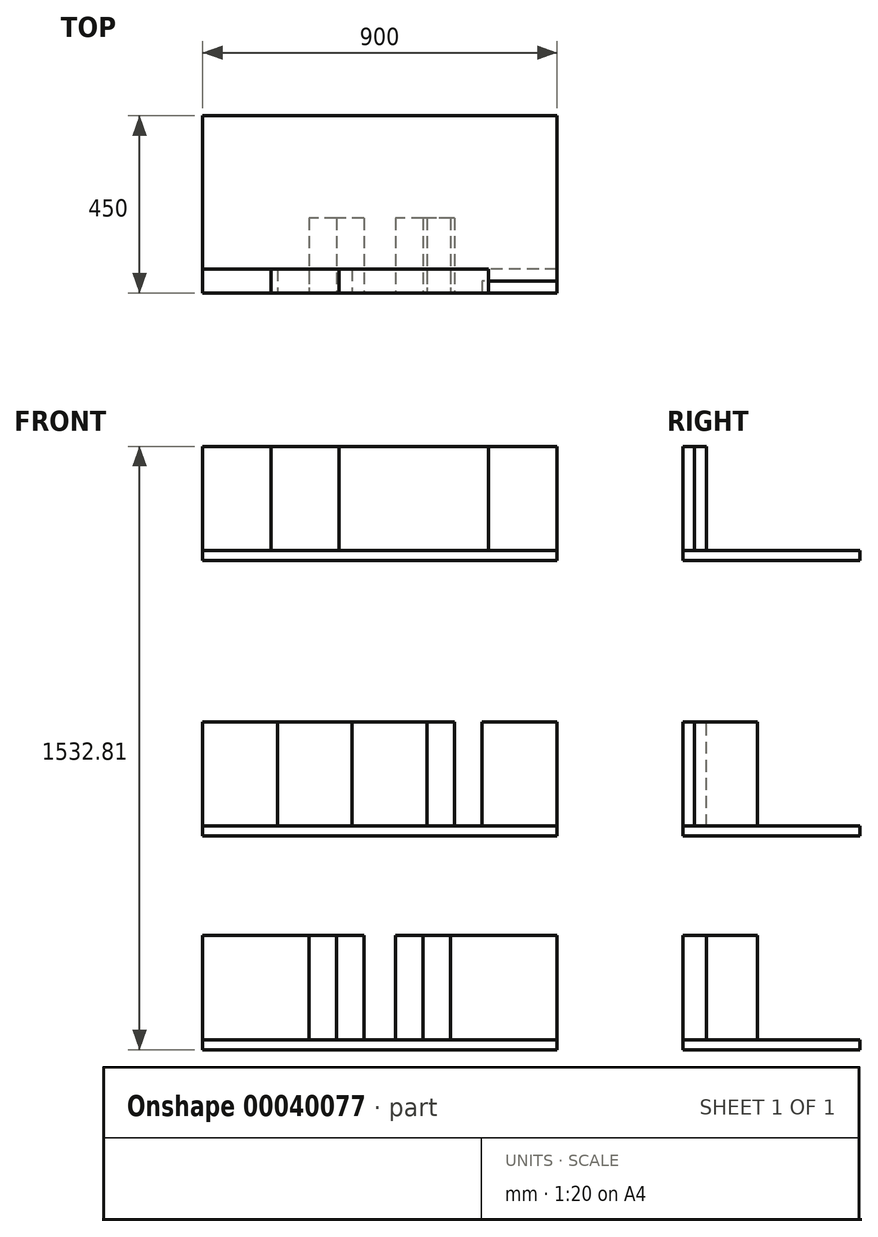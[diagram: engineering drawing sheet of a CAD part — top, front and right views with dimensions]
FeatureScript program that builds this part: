
annotation { "Feature Type Name" : "Feature", "Feature Type Description" : "" }
export const myFeature = defineFeature(function(context is Context, id is Id, definition is map)
    precondition{}
    {
        {
            var Q0;
            Q0=qCreatedBy(makeId("Front.planeOp"),FACE);
            var sketch = newSketch(context, id + "F0", { "sketchPlane" : qUnion([Q0])});
            skLineSegment(sketch, "E0.bottom", {"start": v(483.33, -12.5) * mm, "end": v(-416.67, -12.5) * mm});
            skLineSegment(sketch, "E0.top", {"start": v(483.33, 12.5) * mm, "end": v(-416.67, 12.5) * mm});
            skLineSegment(sketch, "E0.left", {"start": v(483.33, -12.5) * mm, "end": v(483.33, 12.5) * mm});
            skLineSegment(sketch, "E0.right", {"start": v(-416.67, -12.5) * mm, "end": v(-416.67, 12.5) * mm});
            skLineSegment(sketch, "E1.top", {"start": v(-416.67, 277.5) * mm, "end": v(-243.33, 277.5) * mm});
            skLineSegment(sketch, "E1.left", {"start": v(-416.67, 12.5) * mm, "end": v(-416.67, 277.5) * mm});
            skLineSegment(sketch, "E1.right", {"start": v(-243.33, 12.5) * mm, "end": v(-243.33, 277.5) * mm});
            skLineSegment(sketch, "E2.bottom", {"start": v(-243.33, 12.5) * mm, "end": v(-70, 12.5) * mm});
            skLineSegment(sketch, "E2.top", {"start": v(-243.33, 277.5) * mm, "end": v(-70, 277.5) * mm});
            skLineSegment(sketch, "E2.right", {"start": v(-70, 12.5) * mm, "end": v(-70, 277.5) * mm});
            skLineSegment(sketch, "E3.bottom", {"start": v(-70, 12.5) * mm, "end": v(310, 12.5) * mm});
            skLineSegment(sketch, "E3.top", {"start": v(-70, 277.5) * mm, "end": v(310, 277.5) * mm});
            skLineSegment(sketch, "E3.right", {"start": v(310, 12.5) * mm, "end": v(310, 277.5) * mm});
            skLineSegment(sketch, "E4.bottom", {"start": v(310, 277.5) * mm, "end": v(483.33, 277.5) * mm});
            skLineSegment(sketch, "E4.top", {"start": v(310, 12.5) * mm, "end": v(483.33, 12.5) * mm});
            skLineSegment(sketch, "E4.left", {"start": v(310, 277.5) * mm, "end": v(310, 12.5) * mm});
            skLineSegment(sketch, "E4.right", {"start": v(483.33, 277.5) * mm, "end": v(483.33, 12.5) * mm});
            skLineSegment(sketch, "E5.bottom", {"start": v(483.33, -712.13) * mm, "end": v(-416.67, -712.13) * mm});
            skLineSegment(sketch, "E5.top", {"start": v(483.33, -687.13) * mm, "end": v(-416.67, -687.13) * mm});
            skLineSegment(sketch, "E5.left", {"start": v(483.33, -712.13) * mm, "end": v(483.33, -687.13) * mm});
            skLineSegment(sketch, "E5.right", {"start": v(-416.67, -712.13) * mm, "end": v(-416.67, -687.13) * mm});
            skLineSegment(sketch, "E6.top", {"start": v(-416.67, -422.13) * mm, "end": v(-226.67, -422.13) * mm});
            skLineSegment(sketch, "E6.left", {"start": v(-416.67, -687.13) * mm, "end": v(-416.67, -422.13) * mm});
            skLineSegment(sketch, "E6.right", {"start": v(-226.67, -687.13) * mm, "end": v(-226.67, -422.13) * mm});
            skLineSegment(sketch, "E7.bottom", {"start": v(-226.67, -687.13) * mm, "end": v(-36.67, -687.13) * mm});
            skLineSegment(sketch, "E7.top", {"start": v(-226.67, -422.13) * mm, "end": v(-36.67, -422.13) * mm});
            skLineSegment(sketch, "E7.right", {"start": v(-36.67, -687.13) * mm, "end": v(-36.67, -422.13) * mm});
            skLineSegment(sketch, "E8.bottom", {"start": v(-36.67, -687.13) * mm, "end": v(293.33, -687.13) * mm});
            skLineSegment(sketch, "E8.right", {"start": v(293.33, -687.13) * mm, "end": v(293.33, -422.13) * mm});
            skLineSegment(sketch, "E9.bottom", {"start": v(293.33, -422.13) * mm, "end": v(483.33, -422.13) * mm});
            skLineSegment(sketch, "E9.top", {"start": v(293.33, -687.13) * mm, "end": v(483.33, -687.13) * mm});
            skLineSegment(sketch, "E9.left", {"start": v(293.33, -422.13) * mm, "end": v(293.33, -687.13) * mm});
            skLineSegment(sketch, "E9.right", {"start": v(483.33, -422.13) * mm, "end": v(483.33, -687.13) * mm});
            skLineSegment(sketch, "E10", {"start": v(-36.67, -422.13) * mm, "end": v(153.33, -422.13) * mm});
            skLineSegment(sketch, "E11", {"start": v(153.33, -422.13) * mm, "end": v(153.33, -687.13) * mm});
            skLineSegment(sketch, "E12.bottom", {"start": v(153.33, -687.13) * mm, "end": v(223.33, -687.13) * mm});
            skLineSegment(sketch, "E12.top", {"start": v(153.33, -422.13) * mm, "end": v(223.33, -422.13) * mm});
            skLineSegment(sketch, "E12.left", {"start": v(153.33, -687.13) * mm, "end": v(153.33, -422.13) * mm});
            skLineSegment(sketch, "E12.right", {"start": v(223.33, -687.13) * mm, "end": v(223.33, -422.13) * mm});
            skLineSegment(sketch, "E13.bottom", {"start": v(483.33, -1255.31) * mm, "end": v(-416.67, -1255.31) * mm});
            skLineSegment(sketch, "E13.top", {"start": v(483.33, -1230.31) * mm, "end": v(-416.67, -1230.31) * mm});
            skLineSegment(sketch, "E13.left", {"start": v(483.33, -1255.31) * mm, "end": v(483.33, -1230.31) * mm});
            skLineSegment(sketch, "E13.right", {"start": v(-416.67, -1255.31) * mm, "end": v(-416.67, -1230.31) * mm});
            skLineSegment(sketch, "E14.top", {"start": v(-416.67, -965.31) * mm, "end": v(-146.67, -965.31) * mm});
            skLineSegment(sketch, "E14.left", {"start": v(-416.67, -1230.31) * mm, "end": v(-416.67, -965.31) * mm});
            skLineSegment(sketch, "E14.right", {"start": v(-146.67, -1230.31) * mm, "end": v(-146.67, -965.31) * mm});
            skLineSegment(sketch, "E15.bottom", {"start": v(-146.67, -1230.31) * mm, "end": v(-76.67, -1230.31) * mm});
            skLineSegment(sketch, "E15.top", {"start": v(-146.67, -965.31) * mm, "end": v(-76.67, -965.31) * mm});
            skLineSegment(sketch, "E15.right", {"start": v(-76.67, -1230.31) * mm, "end": v(-76.67, -965.31) * mm});
            skLineSegment(sketch, "E16.bottom", {"start": v(-76.67, -1230.31) * mm, "end": v(-6.67, -1230.31) * mm});
            skLineSegment(sketch, "E16.top", {"start": v(-76.67, -965.31) * mm, "end": v(-6.67, -965.31) * mm});
            skLineSegment(sketch, "E16.right", {"start": v(-6.67, -1230.31) * mm, "end": v(-6.67, -965.31) * mm});
            skLineSegment(sketch, "E17", {"start": v(33.33, -1230.31) * mm, "end": v(33.33, -895.3) * mm, "construction": true});
            skLineSegment(sketch, "E18.MirrorCS", {"start": v(73.33, -1230.31) * mm, "end": v(73.33, -965.31) * mm});
            skLineSegment(sketch, "E19.MirrorCS", {"start": v(143.33, -965.31) * mm, "end": v(73.33, -965.31) * mm});
            skLineSegment(sketch, "E20.MirrorCS", {"start": v(143.33, -1230.31) * mm, "end": v(143.33, -965.31) * mm});
            skLineSegment(sketch, "E21.MirrorCS", {"start": v(213.33, -965.31) * mm, "end": v(143.33, -965.31) * mm});
            skLineSegment(sketch, "E22.MirrorCS", {"start": v(213.33, -1230.31) * mm, "end": v(213.33, -965.31) * mm});
            skLineSegment(sketch, "E23.MirrorCS", {"start": v(483.33, -965.31) * mm, "end": v(213.33, -965.31) * mm});
            skLineSegment(sketch, "E24.MirrorCS", {"start": v(483.33, -1230.31) * mm, "end": v(483.33, -965.31) * mm});
            skSolve(sketch);
        }
        {
            var Q0;
            Q0=makeQuery(id+"F0.imprint","IMPRINT",FACE,{"disambiguationData":[TD([[makeQuery(id+"F0.imprint","IMPRINT",EDGE,{"derivedFrom":sQuery(id+"F0.wireOp",EDGE,"E0.bottom")}),-1.0]])]});
            var Q1;
            Q1=makeQuery(id+"F0.imprint","IMPRINT",FACE,{"disambiguationData":[TD([[makeQuery(id+"F0.imprint","IMPRINT",EDGE,{"derivedFrom":sQuery(id+"F0.wireOp",EDGE,"E5.bottom")}),-1.0]])]});
            var Q2;
            Q2=makeQuery(id+"F0.imprint","IMPRINT",FACE,{"disambiguationData":[TD([[makeQuery(id+"F0.imprint","IMPRINT",EDGE,{"derivedFrom":sQuery(id+"F0.wireOp",EDGE,"E13.bottom")}),-1.0]])]});
            extrude(context, id + "F1", {"entities" : qUnion([Q0, Q1, Q2]), "oppositeDirection" : true, "depth" : 450 * mm, "offsetDistance" : 25 * mm});
        }
        {
            var Q0;
            Q0=makeQuery(id+"F0.imprint","IMPRINT",FACE,{"disambiguationData":[TD([[makeQuery(id+"F0.imprint","IMPRINT",EDGE,{"derivedFrom":sQuery(id+"F0.wireOp",EDGE,"E1.top")}),-1.0]])]});
            var Q1;
            Q1=makeQuery(id+"F0.imprint","IMPRINT",FACE,{"disambiguationData":[TD([[makeQuery(id+"F0.imprint","IMPRINT",EDGE,{"derivedFrom":sQuery(id+"F0.wireOp",EDGE,"E6.top")}),-1.0]])]});
            var Q2;
            {var subQ2=sQuery(id+"F0.wireOp",EDGE,"E7.right");Q2=makeQuery(id+"F0.imprint","IMPRINT",FACE,{"disambiguationData":[TD([[makeQuery(id+"F0.imprint","IMPRINT",EDGE,{"derivedFrom":subQ2}),-1.0]])]});}
            var Q3;
            Q3=makeQuery(id+"F0.imprint","IMPRINT",FACE,{"disambiguationData":[TD([[makeQuery(id+"F0.imprint","IMPRINT",EDGE,{"derivedFrom":sQuery(id+"F0.wireOp",EDGE,"E14.top")}),-1.0]])]});
            var Q4;
            {var subQ2=sQuery(id+"F0.wireOp",EDGE,"E22.MirrorCS");Q4=makeQuery(id+"F0.imprint","IMPRINT",FACE,{"disambiguationData":[TD([[makeQuery(id+"F0.imprint","IMPRINT",EDGE,{"derivedFrom":subQ2}),-1.0]])]});}
            extrude(context, id + "F2", {"entities" : qUnion([Q0, Q1, Q2, Q3, Q4]), "oppositeDirection" : true, "depth" : 60 * mm, "offsetDistance" : 25 * mm});
        }
        {
            var Q0;
            {var subQ0=sQuery(id+"F0.wireOp",EDGE,"E1.right");Q0=makeQuery(id+"F0.imprint","IMPRINT",FACE,{"disambiguationData":[TD([[makeQuery(id+"F0.imprint","IMPRINT",EDGE,{"derivedFrom":subQ0}),-1.0]])]});}
            extrude(context, id + "F3", {"entities" : qUnion([Q0]), "oppositeDirection" : true, "depth" : 60 * mm, "offsetDistance" : 25 * mm});
        }
        {
            var Q0;
            {var subQ2=sQuery(id+"F0.wireOp",EDGE,"E2.right");Q0=makeQuery(id+"F0.imprint","IMPRINT",FACE,{"disambiguationData":[TD([[makeQuery(id+"F0.imprint","IMPRINT",EDGE,{"derivedFrom":subQ2}),-1.0]])]});}
            extrude(context, id + "F4", {"entities" : qUnion([Q0]), "oppositeDirection" : true, "depth" : 60 * mm, "offsetDistance" : 25 * mm});
        }
        {
            var Q0;
            {var subQ0=sQuery(id+"F0.wireOp",EDGE,"E3.right");Q0=makeQuery(id+"F0.imprint","IMPRINT",FACE,{"disambiguationData":[TD([[makeQuery(id+"F0.imprint","IMPRINT",EDGE,{"derivedFrom":subQ0}),-1.0]])]});}
            var Q1;
            {var subQ2=sQuery(id+"F0.wireOp",EDGE,"E8.right");Q1=makeQuery(id+"F0.imprint","IMPRINT",FACE,{"disambiguationData":[TD([[makeQuery(id+"F0.imprint","IMPRINT",EDGE,{"derivedFrom":subQ2}),-1.0]])]});}
            extrude(context, id + "F5", {"entities" : qUnion([Q0, Q1]), "oppositeDirection" : true, "depth" : 30 * mm, "offsetDistance" : 25 * mm});
        }
        {
            var Q0;
            {var subQ0=sQuery(id+"F0.wireOp",EDGE,"E6.right");Q0=makeQuery(id+"F0.imprint","IMPRINT",FACE,{"disambiguationData":[TD([[makeQuery(id+"F0.imprint","IMPRINT",EDGE,{"derivedFrom":subQ0}),-1.0]])]});}
            extrude(context, id + "F6", {"entities" : qUnion([Q0]), "oppositeDirection" : true, "depth" : 60 * mm, "offsetDistance" : 25 * mm});
        }
        {
            var Q0;
            {var subQ0=sQuery(id+"F0.wireOp",EDGE,"E11");Q0=makeQuery(id+"F0.imprint","IMPRINT",FACE,{"disambiguationData":[TD([[makeQuery(id+"F0.imprint","IMPRINT",EDGE,{"derivedFrom":subQ0}),1.0]])]});}
            var Q1;
            {var subQ0=sQuery(id+"F0.wireOp",EDGE,"E14.right");Q1=makeQuery(id+"F0.imprint","IMPRINT",FACE,{"disambiguationData":[TD([[makeQuery(id+"F0.imprint","IMPRINT",EDGE,{"derivedFrom":subQ0}),-1.0]])]});}
            var Q2;
            {var subQ0=sQuery(id+"F0.wireOp",EDGE,"E20.MirrorCS");Q2=makeQuery(id+"F0.imprint","IMPRINT",FACE,{"disambiguationData":[TD([[makeQuery(id+"F0.imprint","IMPRINT",EDGE,{"derivedFrom":subQ0}),-1.0]])]});}
            extrude(context, id + "F7", {"entities" : qUnion([Q0, Q1, Q2]), "oppositeDirection" : true, "depth" : 190 * mm, "offsetDistance" : 25 * mm});
        }
        {
            var Q0;
            {var subQ0=sQuery(id+"F0.wireOp",EDGE,"E15.right");Q0=makeQuery(id+"F0.imprint","IMPRINT",FACE,{"disambiguationData":[TD([[makeQuery(id+"F0.imprint","IMPRINT",EDGE,{"derivedFrom":subQ0}),-1.0]])]});}
            var Q1;
            {var subQ0=sQuery(id+"F0.wireOp",EDGE,"E18.MirrorCS");Q1=makeQuery(id+"F0.imprint","IMPRINT",FACE,{"disambiguationData":[TD([[makeQuery(id+"F0.imprint","IMPRINT",EDGE,{"derivedFrom":subQ0}),-1.0]])]});}
            extrude(context, id + "F8", {"entities" : qUnion([Q0, Q1]), "oppositeDirection" : true, "depth" : 190 * mm, "offsetDistance" : 25 * mm});
        }
    });
